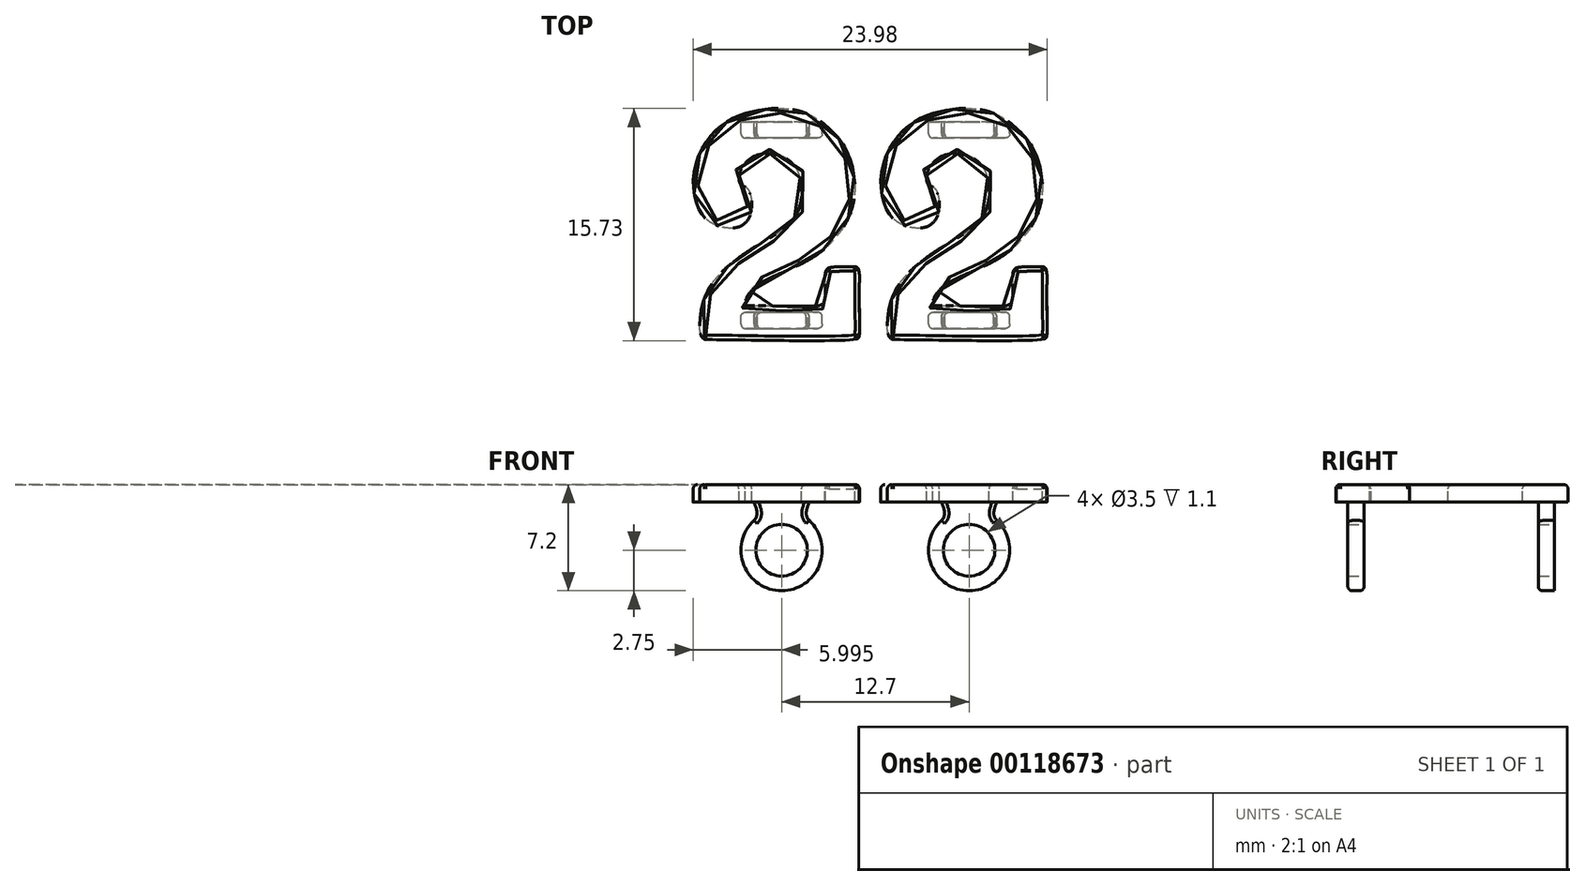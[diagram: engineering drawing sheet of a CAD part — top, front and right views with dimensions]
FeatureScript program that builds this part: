
annotation { "Feature Type Name" : "Feature", "Feature Type Description" : "" }
export const myFeature = defineFeature(function(context is Context, id is Id, definition is map)
    precondition{}
    {
        {
            var Q0;
            Q0=qCreatedBy(makeId("Top.planeOp"),FACE);
            var sketch = newSketch(context, id + "F0", { "sketchPlane" : qUnion([Q0])});
            skLineSegment(sketch, "E0.bottom", {"start": v(-6.6, 7.1) * mm, "end": v(6.6, 7.1) * mm, "construction": true});
            skLineSegment(sketch, "E0.top", {"start": v(-6.6, -7.1) * mm, "end": v(6.6, -7.1) * mm, "construction": true});
            skLineSegment(sketch, "E0.left", {"start": v(-6.6, 7.1) * mm, "end": v(-6.6, -7.1) * mm, "construction": true});
            skLineSegment(sketch, "E0.right", {"start": v(6.6, 7.1) * mm, "end": v(6.6, -7.1) * mm, "construction": true});
            skPoint(sketch, "E0.middle", {"position": v(0, 0) * mm});
            skFitSpline(sketch, "E1", {"points": [v(4.63, -3.8) * mm, v(4.63, -6.2) * mm, v(4.28, -6.46) * mm, v(-3.97, -6.46) * mm, v(-4.1, -6.45) * mm, v(-4.25, -6.31) * mm, v(-4.36, -5.45) * mm, v(-3.83, -3.52) * mm, v(-1.9, -1.65) * mm, v(-0.32, -0.67) * mm, v(1.07, 0.56) * mm, v(1.37, 2.24) * mm, v(1.05, 3.25) * mm, v(0.38, 3.84) * mm, v(-0.42, 4.02) * mm, v(-1.25, 3.91) * mm, v(-1.94, 3.3) * mm, v(-2.16, 2.66) * mm, v(-2.04, 2.28) * mm, v(-1.75, 2.14) * mm, v(-1.47, 1.57) * mm, v(-1.56, 0.44) * mm, v(-2.43, -0.16) * mm, v(-3.74, 0.16) * mm, v(-4.42, 0.95) * mm, v(-4.73, 2.71) * mm, v(-4, 4.71) * mm, v(-2.75, 5.88) * mm, v(-1.33, 6.44) * mm, v(0, 6.6) * mm, v(1.67, 6.3) * mm, v(3.4, 5) * mm, v(4.22, 3.38) * mm, v(4.26, 1.08) * mm, v(3.16, -0.86) * mm, v(1.76, -1.97) * mm, v(0.14, -2.74) * mm, v(-1, -3.3) * mm, v(-1.63, -3.92) * mm, v(-1.8, -4.43) * mm, v(-1.75, -4.52) * mm, v(-1.45, -4.53) * mm, v(2.31, -4.56) * mm, v(2.52, -4.47) * mm, v(2.64, -4.34) * mm, v(2.72, -3.12) * mm, v(2.73, -2.63) * mm, v(2.81, -2.49) * mm, v(2.99, -2.4) * mm, v(4.3, -2.34) * mm, v(4.5, -2.37) * mm, v(4.61, -2.58) * mm, v(4.63, -3.8) * mm]});
            skSolve(sketch);
        }
        {
            var Q0;
            Q0 = qSketchRegion(id + "F0", true);
            extrude(context, id + "F1", {"entities" : qUnion([Q0]), "oppositeDirection" : true, "depth" : 1 * mm, "offsetDistance" : 25 * mm});
        }
        {
            var Q0;
            Q0=makeQuery(id+"F1.opExtrude","SWEPT_BODY",BODY,{"disambiguationData":[OSD([sQuery(id+"F0.wireOp",EDGE,"E1")])]});
            var Q1;
            Q1=qCreatedBy(makeId("Origin.pointOp"),VERTEX);
            transform(context, id + "F2", {"entities" : qUnion([Q0]), "transformType" : TransformType.SCALE_UNIFORMLY, "scale" : 1.2, "scalePoint" : qUnion([Q1]), "makeCopy" : false});
        }
        {
            var Q0;
            Q0=makeQuery(id+"F1.opExtrude","CAP_FACE",FACE,{"disambiguationData":[OSD([sQuery(id+"F0.wireOp",EDGE,"E1")])],"isStart":true});
            fillet(context, id + "F3", {"entities" : qUnion([Q0]), "tangentPropagation" : true, "radius" : 0.3 * mm, "defaultsChanged" : true, "vertexSettings" : [], "allowEdgeOverflow" : false});
        }
        {
            var Q0;
            Q0=makeQuery(id+"F1.opExtrude","CAP_FACE",FACE,{"disambiguationData":[OSD([sQuery(id+"F0.wireOp",EDGE,"E1")])],"isStart":false});
            var sketch = newSketch(context, id + "F4", { "sketchPlane" : qUnion([Q0])});
            skLineSegment(sketch, "E2.bottom", {"start": v(3.05, -7) * mm, "end": v(-2.45, -7) * mm, "construction": true});
            skLineSegment(sketch, "E2.top", {"start": v(3.05, 7) * mm, "end": v(-2.45, 7) * mm, "construction": true});
            skLineSegment(sketch, "E2.left", {"start": v(3.05, -7) * mm, "end": v(3.05, 7) * mm, "construction": true});
            skLineSegment(sketch, "E2.right", {"start": v(-2.45, -7) * mm, "end": v(-2.45, 7) * mm, "construction": true});
            skPoint(sketch, "E2.middle", {"position": v(0.3, 0) * mm});
            skLineSegment(sketch, "E3.bottom", {"start": v(-2.45, 7) * mm, "end": v(3.05, 7) * mm});
            skLineSegment(sketch, "E3.top", {"start": v(-2.45, 5.9) * mm, "end": v(3.05, 5.9) * mm});
            skLineSegment(sketch, "E3.left", {"start": v(-2.45, 7) * mm, "end": v(-2.45, 5.9) * mm});
            skLineSegment(sketch, "E3.right", {"start": v(3.05, 7) * mm, "end": v(3.05, 5.9) * mm});
            skLineSegment(sketch, "E4.bottom", {"start": v(3.05, -7) * mm, "end": v(-2.45, -7) * mm});
            skLineSegment(sketch, "E4.top", {"start": v(3.05, -5.9) * mm, "end": v(-2.45, -5.9) * mm});
            skLineSegment(sketch, "E4.left", {"start": v(3.05, -7) * mm, "end": v(3.05, -5.9) * mm});
            skLineSegment(sketch, "E4.right", {"start": v(-2.45, -7) * mm, "end": v(-2.45, -5.9) * mm});
            skSolve(sketch);
        }
        {
            var Q0;
            Q0=makeQuery(id+"F4.imprint","IMPRINT",FACE,{"disambiguationData":[TD([[makeQuery(id+"F4.imprint","IMPRINT",EDGE,{"derivedFrom":sQuery(id+"F4.wireOp",EDGE,"E3.bottom")}),-1.0]])]});
            var Q1;
            {var subQ1=sQuery(id+"F4.wireOp",EDGE,"E4.top");Q1=makeQuery(id+"F4.imprint","IMPRINT",FACE,{"disambiguationData":[TD([[makeQuery(id+"F4.imprint","IMPRINT",EDGE,{"derivedFrom":subQ1}),1.0]])]});}
            var Q2;
            {var subQ0=sQuery(id+"F4.wireOp",EDGE,"E4.left");var subQ1=sQuery(id+"F4.wireOp",EDGE,"E4.bottom");var subQ2=makeQuery(id+"F4.imprint","INTERSECT",VERTEX,{"derivedFrom":[subQ1,subQ0]});Q2=makeQuery(id+"F4.imprint","IMPRINT",FACE,{"disambiguationData":[TD([[makeQuery(id+"F4.imprint","IMPRINT",EDGE,{"disambiguationData":[TD([[subQ2,-1.0]])],"derivedFrom":subQ1}),-1.0]])]});}
            var Q3;
            {var subQ0=sQuery(id+"F4.wireOp",EDGE,"E4.right");var subQ1=sQuery(id+"F4.wireOp",EDGE,"E4.bottom");var subQ2=makeQuery(id+"F4.imprint","INTERSECT",VERTEX,{"derivedFrom":[subQ1,subQ0]});Q3=makeQuery(id+"F4.imprint","IMPRINT",FACE,{"disambiguationData":[TD([[makeQuery(id+"F4.imprint","IMPRINT",EDGE,{"disambiguationData":[TD([[subQ2,1.0]])],"derivedFrom":subQ1}),-1.0]])]});}
            extrude(context, id + "F5", {"entities" : qUnion([Q0, Q1, Q2, Q3]), "operationType" : NewBodyOperationType.ADD, "depth" : 6 * mm, "offsetDistance" : 25 * mm});
        }
        {
            var Q0;
            Q0=makeQuery(id+"F5.opExtrude","SWEPT_FACE",FACE,{"disambiguationData":[OSD([sQuery(id+"F4.wireOp",EDGE,"E4.bottom")])]});
            var sketch = newSketch(context, id + "F6", { "sketchPlane" : qUnion([Q0])});
            skPoint(sketch, "E5.0", {"position": v(-2.25, -1.2) * mm});
            skLineSegment(sketch, "E6.0.0", {"start": v(-2.25, -1.2) * mm, "end": v(-3.05, -1.2) * mm});
            skLineSegment(sketch, "E6.0.1", {"start": v(-3.05, -1.2) * mm, "end": v(-3.05, -4.45) * mm});
            skLineSegment(sketch, "E6.0.2", {"start": v(-0.3, -7.2) * mm, "end": v(-0.3, -7.2) * mm});
            skLineSegment(sketch, "E6.0.3", {"start": v(2.45, -4.45) * mm, "end": v(2.45, -1.2) * mm});
            skLineSegment(sketch, "E6.0.4", {"start": v(2.45, -1.2) * mm, "end": v(-2.25, -1.2) * mm});
            skLineSegment(sketch, "E6.0.5", {"start": v(-2.25, -1.2) * mm, "end": v(-2.25, -1.2) * mm});
            skPoint(sketch, "E7.visualSharp", {"position": v(2.45, -7.2) * mm});
            skArc(sketch, "E7.filletArc", {"start": v(-0.3, -7.2) * mm, "mid": v(1.64, -6.4) * mm, "end": v(2.45, -4.45) * mm});
            skPoint(sketch, "E8.visualSharp", {"position": v(-3.05, -7.2) * mm});
            skArc(sketch, "E8.filletArc", {"start": v(-3.05, -4.45) * mm, "mid": v(-2.25, -6.4) * mm, "end": v(-0.3, -7.2) * mm});
            skCircle(sketch, "E9", {"center": v(-0.3, -4.45) * mm, "radius": 1.75 * mm});
            skArc(sketch, "E10", {"start": v(2.45, -4.45) * mm, "mid": v(2.22, -3.35) * mm, "end": v(1.57, -2.44) * mm});
            skFitSpline(sketch, "E11", {"points": [v(1.57, -2.44) * mm, v(1.36, -2.02) * mm, v(1.57, -1.2) * mm], "startDerivative": vector(-1, 1.12) * mm, "endDerivative": vector(0.91, 2.26) * mm});
            skLineSegment(sketch, "E12", {"start": v(-0.3, -4.45) * mm, "end": v(-0.3, -1.2) * mm, "construction": true});
            skArc(sketch, "E13.MirrorCS", {"start": v(-3.05, -4.45) * mm, "mid": v(-2.83, -3.35) * mm, "end": v(-2.18, -2.44) * mm});
            skFitSpline(sketch, "E14.MirrorCS", {"points": [v(-2.18, -2.44) * mm, v(-1.97, -2.02) * mm, v(-2.18, -1.2) * mm], "startDerivative": vector(1, 1.12) * mm, "endDerivative": vector(-0.91, 2.26) * mm});
            skSolve(sketch);
        }
        {
            var Q0;
            {var subQ0=sQuery(id+"F6.wireOp",EDGE,"E7.filletArc");Q0=makeQuery(id+"F6.imprint","IMPRINT",FACE,{"disambiguationData":[TD([[makeQuery(id+"F6.imprint","IMPRINT",EDGE,{"derivedFrom":subQ0}),-1.0]])]});}
            var Q1;
            {var subQ0=sQuery(id+"F6.wireOp",EDGE,"E8.filletArc");Q1=makeQuery(id+"F6.imprint","IMPRINT",FACE,{"disambiguationData":[TD([[makeQuery(id+"F6.imprint","IMPRINT",EDGE,{"derivedFrom":subQ0}),-1.0]])]});}
            var Q2;
            Q2=makeQuery(id+"F6.imprint","IMPRINT",FACE,{"disambiguationData":[TD([[makeQuery(id+"F6.imprint","IMPRINT",EDGE,{"derivedFrom":sQuery(id+"F6.wireOp",EDGE,"E6.0.0")}),-1.0]])]});
            var Q3;
            {var subQ0=sQuery(id+"F6.wireOp",EDGE,"E6.0.3");Q3=makeQuery(id+"F6.imprint","IMPRINT",FACE,{"disambiguationData":[TD([[makeQuery(id+"F6.imprint","IMPRINT",EDGE,{"derivedFrom":subQ0}),1.0]])]});}
            var Q4;
            Q4=makeQuery(id+"F6.imprint","IMPRINT",FACE,{"disambiguationData":[TD([[makeQuery(id+"F6.imprint","IMPRINT",EDGE,{"derivedFrom":sQuery(id+"F6.wireOp",EDGE,"E9")}),1.0]])]});
            extrude(context, id + "F7", {"entities" : qUnion([Q0, Q1, Q2, Q3, Q4]), "operationType" : NewBodyOperationType.REMOVE, "oppositeDirection" : true, "depth" : 25 * mm, "offsetDistance" : 25 * mm});
        }
        {
            var Q0;
            Q0=makeQuery(id+"F7.boolean.opBoolean","MERGE",EDGE,{"derivedFrom":[],"fromTools":[makeQuery(id+"F7.opExtrude","CAP_EDGE",EDGE,{"disambiguationData":[OSD([sQuery(id+"F6.wireOp",EDGE,"E7.filletArc")])],"isStart":true}),makeQuery(id+"F7.opExtrude","CAP_EDGE",EDGE,{"disambiguationData":[OSD([sQuery(id+"F6.wireOp",EDGE,"E8.filletArc")])],"isStart":true}),makeQuery(id+"F7.opExtrude","CAP_EDGE",EDGE,{"disambiguationData":[OSD([sQuery(id+"F6.wireOp",EDGE,"E10")])],"isStart":true}),makeQuery(id+"F7.opExtrude","CAP_EDGE",EDGE,{"disambiguationData":[OSD([sQuery(id+"F6.wireOp",EDGE,"E13.MirrorCS")])],"isStart":true})]});
            var Q1;
            Q1=makeQuery(id+"F7.boolean.opBoolean","COPY",EDGE,{"derivedFrom":makeQuery(id+"F7.opExtrude","CAP_EDGE",EDGE,{"disambiguationData":[OSD([sQuery(id+"F6.wireOp",EDGE,"E11")])],"isStart":true})});
            var Q2;
            Q2=makeQuery(id+"F7.boolean.opBoolean","COPY",EDGE,{"derivedFrom":makeQuery(id+"F7.opExtrude","CAP_EDGE",EDGE,{"disambiguationData":[OSD([sQuery(id+"F6.wireOp",EDGE,"E14.MirrorCS")])],"isStart":true})});
            var Q3;
            Q3=makeQuery(id+"F7.boolean.opBoolean","INTERSECT",EDGE,{"derivedFrom":[makeQuery(id+"F5.opExtrude","SWEPT_FACE",FACE,{"disambiguationData":[OSD([sQuery(id+"F4.wireOp",EDGE,"E4.top")])]}),makeQuery(id+"F7.opExtrude","SWEPT_FACE",FACE,{"disambiguationData":[OSD([sQuery(id+"F6.wireOp",EDGE,"E7.filletArc")])]}),makeQuery(id+"F7.opExtrude","SWEPT_FACE",FACE,{"disambiguationData":[OSD([sQuery(id+"F6.wireOp",EDGE,"E8.filletArc")])]}),makeQuery(id+"F7.opExtrude","SWEPT_FACE",FACE,{"disambiguationData":[OSD([sQuery(id+"F6.wireOp",EDGE,"E10")])]}),makeQuery(id+"F7.opExtrude","SWEPT_FACE",FACE,{"disambiguationData":[OSD([sQuery(id+"F6.wireOp",EDGE,"E13.MirrorCS")])]})]});
            var Q4;
            Q4=makeQuery(id+"F7.boolean.opBoolean","INTERSECT",EDGE,{"derivedFrom":[makeQuery(id+"F5.opExtrude","SWEPT_FACE",FACE,{"disambiguationData":[OSD([sQuery(id+"F4.wireOp",EDGE,"E4.top")])]}),makeQuery(id+"F7.opExtrude","SWEPT_FACE",FACE,{"disambiguationData":[OSD([sQuery(id+"F6.wireOp",EDGE,"E14.MirrorCS")])]})]});
            var Q5;
            Q5=makeQuery(id+"F7.boolean.opBoolean","INTERSECT",EDGE,{"derivedFrom":[makeQuery(id+"F5.opExtrude","SWEPT_FACE",FACE,{"disambiguationData":[OSD([sQuery(id+"F4.wireOp",EDGE,"E4.top")])]}),makeQuery(id+"F7.opExtrude","SWEPT_FACE",FACE,{"disambiguationData":[OSD([sQuery(id+"F6.wireOp",EDGE,"E11")])]})]});
            var Q6;
            Q6=makeQuery(id+"F7.boolean.opBoolean","INTERSECT",EDGE,{"derivedFrom":[makeQuery(id+"F5.opExtrude","SWEPT_FACE",FACE,{"disambiguationData":[OSD([sQuery(id+"F4.wireOp",EDGE,"E3.bottom")])]}),makeQuery(id+"F7.opExtrude","SWEPT_FACE",FACE,{"disambiguationData":[OSD([sQuery(id+"F6.wireOp",EDGE,"E14.MirrorCS")])]})]});
            var Q7;
            Q7=makeQuery(id+"F7.boolean.opBoolean","INTERSECT",EDGE,{"derivedFrom":[makeQuery(id+"F5.opExtrude","SWEPT_FACE",FACE,{"disambiguationData":[OSD([sQuery(id+"F4.wireOp",EDGE,"E3.bottom")])]}),makeQuery(id+"F7.opExtrude","SWEPT_FACE",FACE,{"disambiguationData":[OSD([sQuery(id+"F6.wireOp",EDGE,"E7.filletArc")])]}),makeQuery(id+"F7.opExtrude","SWEPT_FACE",FACE,{"disambiguationData":[OSD([sQuery(id+"F6.wireOp",EDGE,"E8.filletArc")])]}),makeQuery(id+"F7.opExtrude","SWEPT_FACE",FACE,{"disambiguationData":[OSD([sQuery(id+"F6.wireOp",EDGE,"E10")])]}),makeQuery(id+"F7.opExtrude","SWEPT_FACE",FACE,{"disambiguationData":[OSD([sQuery(id+"F6.wireOp",EDGE,"E13.MirrorCS")])]})]});
            var Q8;
            Q8=makeQuery(id+"F7.boolean.opBoolean","INTERSECT",EDGE,{"derivedFrom":[makeQuery(id+"F5.opExtrude","SWEPT_FACE",FACE,{"disambiguationData":[OSD([sQuery(id+"F4.wireOp",EDGE,"E3.bottom")])]}),makeQuery(id+"F7.opExtrude","SWEPT_FACE",FACE,{"disambiguationData":[OSD([sQuery(id+"F6.wireOp",EDGE,"E11")])]})]});
            var Q9;
            Q9=makeQuery(id+"F7.boolean.opBoolean","INTERSECT",EDGE,{"derivedFrom":[makeQuery(id+"F5.opExtrude","SWEPT_FACE",FACE,{"disambiguationData":[OSD([sQuery(id+"F4.wireOp",EDGE,"E3.top")])]}),makeQuery(id+"F7.opExtrude","SWEPT_FACE",FACE,{"disambiguationData":[OSD([sQuery(id+"F6.wireOp",EDGE,"E14.MirrorCS")])]})]});
            var Q10;
            Q10=makeQuery(id+"F7.boolean.opBoolean","INTERSECT",EDGE,{"derivedFrom":[makeQuery(id+"F5.opExtrude","SWEPT_FACE",FACE,{"disambiguationData":[OSD([sQuery(id+"F4.wireOp",EDGE,"E3.top")])]}),makeQuery(id+"F7.opExtrude","SWEPT_FACE",FACE,{"disambiguationData":[OSD([sQuery(id+"F6.wireOp",EDGE,"E7.filletArc")])]}),makeQuery(id+"F7.opExtrude","SWEPT_FACE",FACE,{"disambiguationData":[OSD([sQuery(id+"F6.wireOp",EDGE,"E8.filletArc")])]}),makeQuery(id+"F7.opExtrude","SWEPT_FACE",FACE,{"disambiguationData":[OSD([sQuery(id+"F6.wireOp",EDGE,"E10")])]}),makeQuery(id+"F7.opExtrude","SWEPT_FACE",FACE,{"disambiguationData":[OSD([sQuery(id+"F6.wireOp",EDGE,"E13.MirrorCS")])]})]});
            var Q11;
            Q11=makeQuery(id+"F7.boolean.opBoolean","INTERSECT",EDGE,{"derivedFrom":[makeQuery(id+"F5.opExtrude","SWEPT_FACE",FACE,{"disambiguationData":[OSD([sQuery(id+"F4.wireOp",EDGE,"E3.top")])]}),makeQuery(id+"F7.opExtrude","SWEPT_FACE",FACE,{"disambiguationData":[OSD([sQuery(id+"F6.wireOp",EDGE,"E11")])]})]});
            fillet(context, id + "F8", {"entities" : qUnion([Q0, Q1, Q2, Q3, Q4, Q5, Q6, Q7, Q8, Q9, Q10, Q11]), "tangentPropagation" : true, "radius" : 0.3 * mm, "defaultsChanged" : false, "vertexSettings" : [], "allowEdgeOverflow" : false});
        }
        {
            var Q0;
            Q0=makeQuery(id+"F1.opExtrude","SWEPT_BODY",BODY,{"disambiguationData":[OSD([sQuery(id+"F0.wireOp",EDGE,"E1")])]});
            transform(context, id + "F9", {"entities" : qUnion([Q0]), "transformType" : TransformType.TRANSLATION_3D, "dx" : 12.7 * mm, "dy" : 0 * mm, "dz" : 0 * mm, "makeCopy" : true});
        }
    });
